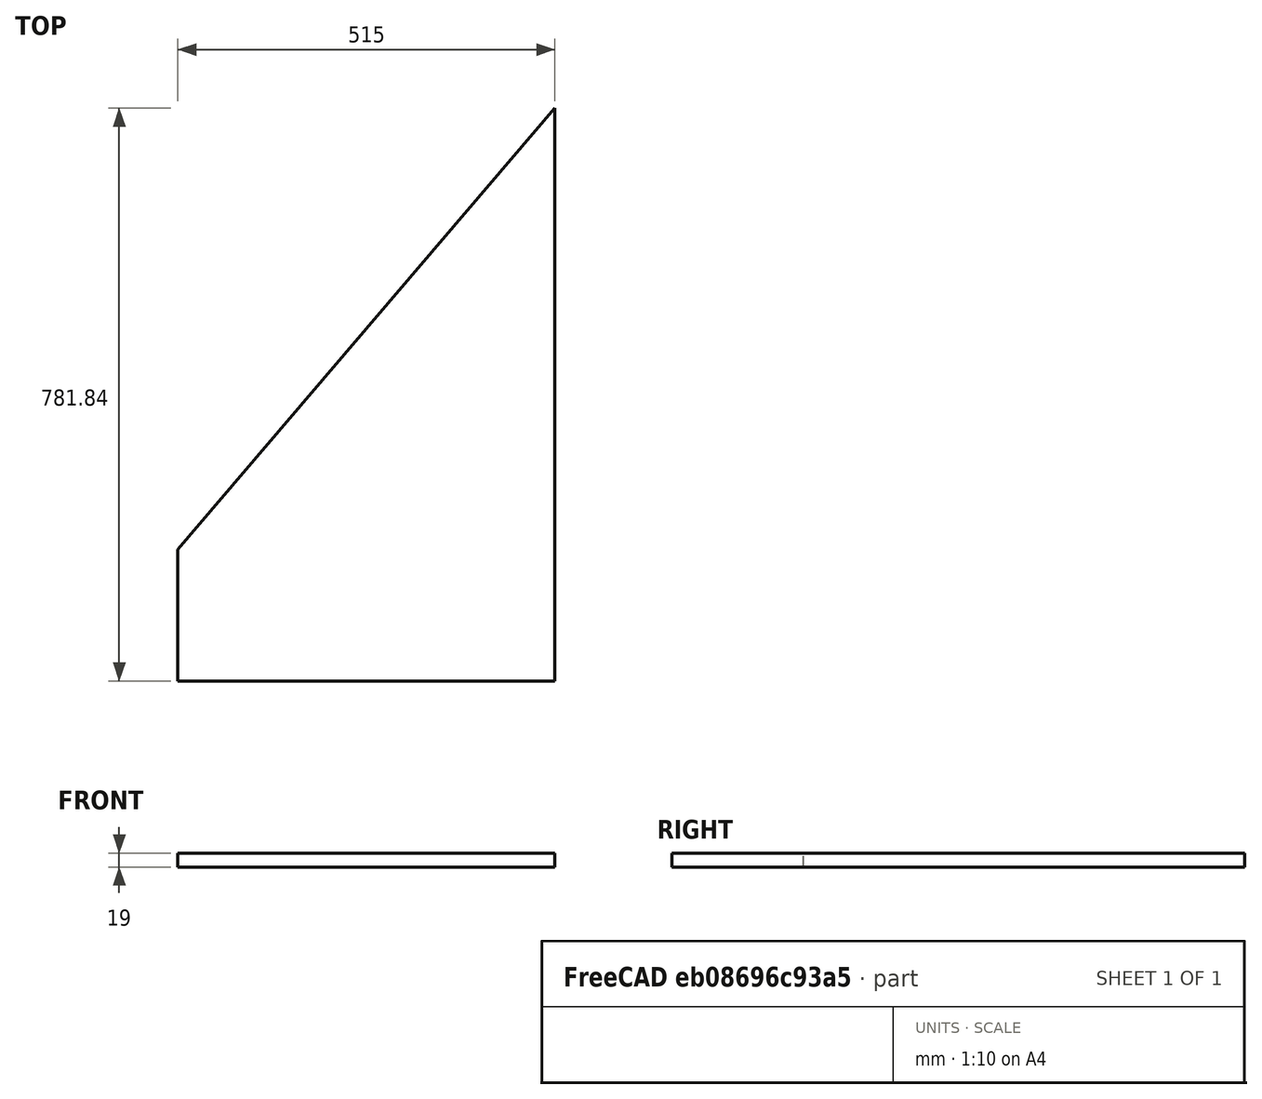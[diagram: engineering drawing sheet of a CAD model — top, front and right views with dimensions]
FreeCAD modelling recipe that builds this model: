
FCSTD DOCUMENT  (FreeCAD 1.0R39285 (Git))
Label: wardrobe_door_03_jan
License: All rights reserved
LicenseURL: https://en.wikipedia.org/wiki/All_rights_reserved
objects: TechDraw::DrawViewDimension×6, PartDesign::CoordinateSystem×2, TechDraw::DrawProjGroupItem×2, Sketcher::SketchObject×1, PartDesign::Pad×1, PartDesign::Body×1, App::Part×1, TechDraw::DrawSVGTemplate×1, TechDraw::DrawViewAnnotation×1, TechDraw::DrawPage×1
note: 15 computed .brp shape members not serialized (recipe doc carries the construction recipe); baked Part::Feature solids carry a one-line shape summary decoded from their .brp
EXTERNAL_REF file=../../mastersketch.FCStd obj=Sketch

FEATURE [Sketcher::SketchObject] Sketch
  ArcFitTolerance = 1e-06
  AttachmentSupport = -> [XY_Plane]
  FullyConstrained = true
  MakeInternals = false
  MapMode = 5
  expr: Constraints[0] = mastersketch#Sketch.Constraints.corpus03_door_height
  expr: Constraints[10] = mastersketch#Sketch.Constraints.alpha
  expr: Constraints[3] = mastersketch#Sketch.Constraints.corpus03_door_width
  sketch-geometry (4):
    g0: LineSegment StartX=0 StartY=0 StartZ=0 EndX=0 EndY=781.837 EndZ=0
    g1: LineSegment StartX=0 StartY=0 StartZ=0 EndX=-515 EndY=0 EndZ=0
    g2: LineSegment StartX=-515 StartY=0 StartZ=0 EndX=-515 EndY=179.234 EndZ=0
    g3: LineSegment StartX=-515 StartY=179.234 StartZ=0 EndX=0 EndY=781.837 EndZ=0
  constraints (11):
    c: Distance(g0) = 781.837
    c: Coincident(g0,g-1)
    c: Vertical(g0)
    c: Distance(g1) = 515
    c: Coincident(g1,g0)
    c: PointOnObject(g1,g-1)
    c: Vertical(g2)
    c: Coincident(g3,g2)
    c: Coincident(g2,g1)
    c: Coincident(g3,g0)
    c: Angle(g2,g3) = 2.43442
FEATURE [PartDesign::Pad] Pad
  Direction = (0,0,1)
  Length = 19
  Length2 = 10
  Profile = -> Sketch
  ReferenceAxis = -> Sketch [N_Axis]
  Refine = true
  Suppressed = false
  Type = 0
FEATURE [PartDesign::Body] Body  label="wardrobe_door_corpus02_jan"
  AllowCompound = false
  Group = -> [Sketch,Pad]
  Origin = -> Origin
  Tip = -> Pad
FEATURE [PartDesign::CoordinateSystem] LCS_2
  AttacherType = Attacher::AttachEngine3D
  AttachmentSupport = -> [Pad]
  MapMode = 7
  Placement = pos=(-515,179.234,0) rot=(0.886496,-0.327204,-0.327204;1.69098rad)
FEATURE [PartDesign::CoordinateSystem] LCS_Origin
  AttacherType = Attacher::AttachEngine3D
  AttachmentSupport = -> [X_Axis001]
  MapMode = 2
FEATURE [App::Part] wardrobe_door_03_jan
  DrawingName = wardrobe_door_03_jan.FCStd
  Group = -> [LCS_Origin,Body,LCS_2]
  Origin = -> Origin001
  PartDescription = wardrobe_door_corpus02_jan
  PartID = wardrobe_door_03_jan
FEATURE [TechDraw::DrawSVGTemplate] Template  label="Vorlage"
  Height = 210
  Orientation = 1
  Template = <userpath>/scoop/apps/freecad/current/data/Mod/TechDraw/Templates/A4_Landscape_TD.svg
  Width = 297
FEATURE [TechDraw::DrawProjGroupItem] View
  CoarseView = false
  Direction = (-2e-16,0,-1)
  Focus = 100
  HardHidden = false
  IsoCount = 0
  IsoHidden = false
  IsoVisible = false
  LockPosition = false
  Perspective = false
  Rotation = 0
  RotationVector = (1,0,0)
  Scale = 0.1
  ScaleType = 2
  ScrubCount = 1
  SeamHidden = false
  SeamVisible = false
  SmoothHidden = false
  SmoothVisible = true
  Source = -> [wardrobe_door_03_jan]
  Type = 0
  X = 138.085
  XDirection = (2e-16,-1,0)
  Y = 151.508
FEATURE [TechDraw::DrawProjGroupItem] View001
  CoarseView = false
  Direction = (-1,1e-16,0)
  Focus = 100
  HardHidden = false
  IsoCount = 0
  IsoHidden = false
  IsoVisible = false
  LockPosition = false
  Perspective = false
  Rotation = 0
  RotationVector = (1,0,0)
  Scale = 0.1
  ScaleType = 2
  ScrubCount = 1
  SeamHidden = false
  SeamVisible = false
  SmoothHidden = false
  SmoothVisible = true
  Source = -> [wardrobe_door_03_jan]
  Type = 0
  X = 138.085
  XDirection = (-1e-16,-1,1e-16)
  Y = 98.1765
FEATURE [TechDraw::DrawViewAnnotation] Annotation  label="Beschriftung"
  Font = MS Shell Dlg 2
  LineSpace = 100
  LockPosition = false
  MaxWidth = -1
  Rotation = 0
  ScaleType = 0
  Text = Rev 01
  TextSize = 5
  TextStyle = 0
  X = 274.352
  Y = 62.5385
FEATURE [TechDraw::DrawViewDimension] Dimension  label="Maß"
  AngleOverride = false
  Arbitrary = false
  ArbitraryTolerances = false
  BoxCorners = (2) [(-39.0919,-25.75,0),(39.0919,25.75,0)]
  EqualTolerance = true
  ExtensionAngle = 0
  FormatSpec = %.1w
  FormatSpecOverTolerance = %+.1w
  FormatSpecUnderTolerance = %+.1w
  Inverted = false
  LineAngle = 0
  LockPosition = false
  MeasureType = 1
  OverTolerance = 0
  References2D = -> [View]
  Rotation = 0
  ScaleType = 0
  TheoreticalExact = false
  Type = 1
  UnderTolerance = 0
  X = 4.16935
  Y = -30.3138
FEATURE [TechDraw::DrawViewDimension] Dimension001  label="Maß001"
  AngleOverride = false
  Arbitrary = false
  ArbitraryTolerances = false
  BoxCorners = (2) [(-39.0919,-25.75,0),(39.0919,25.75,0)]
  EqualTolerance = true
  ExtensionAngle = 0
  FormatSpec = %.1w
  FormatSpecOverTolerance = %+.1w
  FormatSpecUnderTolerance = %+.1w
  Inverted = false
  LineAngle = 0
  LockPosition = false
  MeasureType = 1
  OverTolerance = 0
  References2D = -> [View]
  Rotation = 0
  ScaleType = 0
  TheoreticalExact = false
  Type = 2
  UnderTolerance = 0
  X = 52.2413
  Y = 0
FEATURE [TechDraw::DrawViewDimension] Dimension002  label="Maß002"
  AngleOverride = false
  Arbitrary = false
  ArbitraryTolerances = false
  BoxCorners = (2) [(-39.0919,-25.75,0),(39.0919,25.75,0)]
  EqualTolerance = true
  ExtensionAngle = 0
  FormatSpec = %.1w
  FormatSpecOverTolerance = %+.1w
  FormatSpecUnderTolerance = %+.1w
  Inverted = false
  LineAngle = 0
  LockPosition = false
  MeasureType = 1
  OverTolerance = 0
  References2D = -> [View]
  Rotation = 0
  ScaleType = 0
  TheoreticalExact = false
  Type = 1
  UnderTolerance = 0
  X = 30.1302
  Y = 42.2312
FEATURE [TechDraw::DrawViewDimension] Dimension003  label="Maß003"
  AngleOverride = false
  Arbitrary = false
  ArbitraryTolerances = false
  BoxCorners = (2) [(-39.0919,-25.75,0),(39.0919,25.75,0)]
  EqualTolerance = true
  ExtensionAngle = 0
  FormatSpec = (%.1w)
  FormatSpecOverTolerance = %+.1w
  FormatSpecUnderTolerance = %+.1w
  Inverted = false
  LineAngle = 0
  LockPosition = false
  MeasureType = 1
  OverTolerance = 0
  References2D = -> [View]
  Rotation = 0
  ScaleType = 0
  TheoreticalExact = false
  Type = 6
  UnderTolerance = 0
  X = 24.0227
  Y = 18.1693
FEATURE [TechDraw::DrawViewDimension] Dimension004  label="Maß004"
  AngleOverride = false
  Arbitrary = false
  ArbitraryTolerances = false
  BoxCorners = (2) [(-39.0919,-0.9,0),(39.0919,0.9,0)]
  EqualTolerance = true
  ExtensionAngle = 0
  FormatSpec = %.1w
  FormatSpecOverTolerance = %+.1w
  FormatSpecUnderTolerance = %+.1w
  Inverted = false
  LineAngle = 0
  LockPosition = false
  MeasureType = 1
  OverTolerance = 0
  References2D = -> [View001]
  Rotation = 0
  ScaleType = 0
  TheoreticalExact = false
  Type = 0
  UnderTolerance = 0
  X = 46.5954
  Y = -8.822
FEATURE [TechDraw::DrawViewDimension] Dimension005  label="Maß005"
  AngleOverride = false
  Arbitrary = false
  ArbitraryTolerances = false
  BoxCorners = (2) [(-39.0919,-25.75,0),(39.0919,25.75,0)]
  EqualTolerance = true
  ExtensionAngle = 0
  FormatSpec = (%.1w)
  FormatSpecOverTolerance = %+.1w
  FormatSpecUnderTolerance = %+.1w
  Inverted = false
  LineAngle = 0
  LockPosition = false
  MeasureType = 1
  OverTolerance = 0
  References2D = -> [View]
  Rotation = 0
  ScaleType = 0
  TheoreticalExact = false
  Type = 0
  UnderTolerance = 0
  X = -17.7962
  Y = 15.4858
FEATURE [TechDraw::DrawPage] Page  label="Seite"
  KeepUpdated = true
  NextBalloonIndex = 1
  ProjectionType = 0
  Template = -> Template
  Views = -> [View,View001,Annotation,Dimension,Dimension001,Dimension002,Dimension003,Dimension004,Dimension005]
